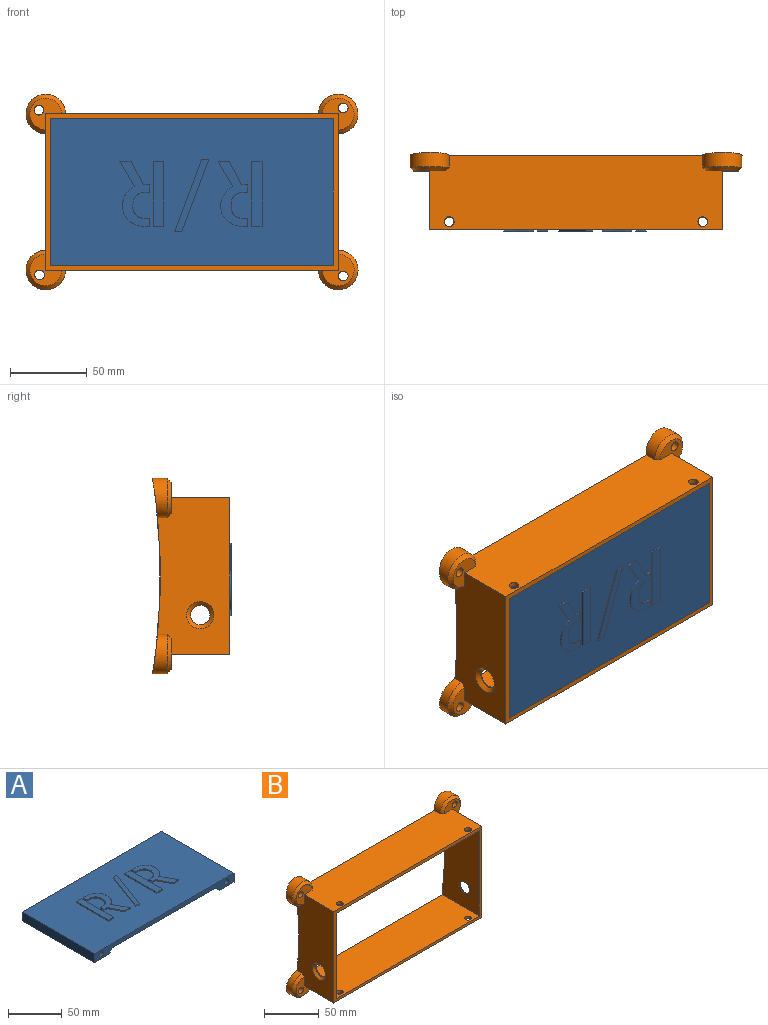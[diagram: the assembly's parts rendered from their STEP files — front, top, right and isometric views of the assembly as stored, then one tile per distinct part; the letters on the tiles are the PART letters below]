
ASSEMBLY  parts=2 mates=1
PART A: 82 faces, bbox 184.2x95.3x11.7 mm
  f0: plane 184.15x95.25mm, normal (0,0,1), area 16051.4mm2, adj f1,f6,f9,f10,f13,f14,f15,f16
  f1: plane 95.25x10.16mm, normal (-1,0,0), area 967.7mm2, adj f0,f2,f9,f10
  f2: plane 95.25x19.05mm, normal (0,0,-1), area 1814.5mm2, adj f1,f9,f10,f12
  f3: plane 135.89x95.25mm, normal (0,0,-1), area 12943.5mm2, adj f9,f10,f11,f12
  f4: plane 95.25x0.22mm, normal (-1,0,0), area 21mm2, adj f5,f9,f10,f11
  f5: plane 95.25x19.05mm, normal (0,0,-1), area 1814.5mm2, adj f4,f6,f9,f10
  f6: plane 95.25x10.38mm, normal (1,0,0), area 988.7mm2, adj f0,f5,f9,f10
  f7: cylinder r=3.17mm len=95.25mm, axis (0,1,0), area 1900.2mm2, adj f9,f10
  f8: cylinder r=3.17mm len=95.25mm, axis (0,1,0), area 1900.2mm2, adj f9,f10
  f9: plane 184.15x10.38mm, normal (0,-1,0), area 1095.7mm2, adj f0,f1,f2,f3,f4,f5,f6,f7
  f10: plane 184.15x10.38mm, normal (0,1,0), area 1095.7mm2, adj f0,f1,f2,f3,f4,f5,f6,f7
  f11: plane 95.25x5.08mm, normal (-0.71,0,-0.71), area 684.3mm2, adj f3,f4,f9,f10
  f12: plane 95.25x5.08mm, normal (0.71,0,-0.71), area 684.3mm2, adj f2,f3,f9,f10
  f13: plane 42.29x1.27mm, normal (-1,0,0), area 53.7mm2, adj f0,f14,f16,f17
  f14: plane 6.89x1.27mm, normal (0,-1,0), area 8.7mm2, adj f0,f13,f15,f17
  f15: plane 42.29x1.27mm, normal (1,0,0), area 53.7mm2, adj f0,f14,f16,f17
  f16: plane 6.89x1.27mm, normal (0,1,0), area 8.7mm2, adj f0,f13,f15,f17
  f17: plane 42.29x6.89mm, normal (0,0,1), area 291.2mm2, adj f13,f14,f15,f16
  f18: plane 16.65x9.64mm, normal (0.87,0.5,0), area 24.4mm2, adj f0,f19,f43,f44
  f19: extruded ~5.73x4.76mm, area 9.6mm2, adj f0,f18,f20,f44
  f20: extruded ~7.8x2.13mm, area 10.4mm2, adj f0,f19,f21,f44
  f21: extruded ~5.49x1.29mm, area 7.2mm2, adj f0,f20,f22,f44
  f22: extruded ~4.16x3.39mm, area 6.9mm2, adj f0,f21,f23,f44
  f23: extruded ~4.74x2.58mm, area 6.9mm2, adj f0,f22,f24,f44
  f24: extruded ~5.33x1.27mm, area 6.9mm2, adj f0,f23,f25,f44
  f25: plane 2.93x1.27mm, normal (0,1,0), area 3.7mm2, adj f0,f24,f26,f44
  f26: plane 5.22x1.27mm, normal (-1,0,0), area 6.6mm2, adj f0,f25,f27,f44
  f27: plane 2.81x1.27mm, normal (0,-1,0), area 3.6mm2, adj f0,f26,f28,f44
  f28: extruded ~4.25x1.27mm, area 5.6mm2, adj f0,f27,f29,f44
  f29: extruded ~2.49x2.07mm, area 4.1mm2, adj f0,f28,f30,f44
  f30: extruded ~2.58x1.27mm, area 3.6mm2, adj f0,f29,f31,f44
  f31: extruded ~2.39x1.27mm, area 3.1mm2, adj f0,f30,f32,f44
  f32: extruded ~4.33x1.27mm, area 5.6mm2, adj f0,f31,f33,f44
  f33: extruded ~2.73x1.67mm, area 4.1mm2, adj f0,f32,f34,f44
  f34: extruded ~2.3x1.4mm, area 3.4mm2, adj f0,f33,f35,f44
  f35: extruded ~2.52x1.27mm, area 3.3mm2, adj f0,f34,f36,f44
  f36: plane 3.9x1.27mm, normal (0,1,0), area 5mm2, adj f0,f35,f37,f44
  f37: plane 5.05x1.27mm, normal (-1,0,0), area 6.4mm2, adj f0,f36,f38,f44
  f38: plane 2.03x1.27mm, normal (0,-1,0), area 2.6mm2, adj f0,f37,f39,f44
  f39: plane 1.27x1.18mm, normal (0,-1,0), area 1.5mm2, adj f0,f38,f40,f44
  f40: extruded ~1.27x0.6mm, area 0.8mm2, adj f0,f39,f41,f44
  f41: extruded ~1.27x0.37mm, area 0.5mm2, adj f0,f40,f42,f44
  f42: plane 15.32x7.98mm, normal (-0.89,-0.46,0), area 21.9mm2, adj f0,f41,f43,f44
  f43: plane 7.29x1.27mm, normal (0,-1,0), area 9.3mm2, adj f0,f18,f42,f44
  f44: plane 42.29x19.46mm, normal (0,0,1), area 343.7mm2, adj f18,f19,f20,f21,f22,f23,f24,f25
  f45: plane 47.12x17.62mm, normal (0.94,-0.35,0), area 63.9mm2, adj f0,f46,f48,f49
  f46: plane 4.66x1.27mm, normal (0,1,0), area 5.9mm2, adj f0,f45,f47,f49
  f47: plane 47.12x17.61mm, normal (-0.94,0.35,0), area 63.9mm2, adj f0,f46,f48,f49
  f48: plane 4.65x1.27mm, normal (0,-1,0), area 5.9mm2, adj f0,f45,f47,f49
  f49: plane 47.12x22.27mm, normal (0,0,1), area 219.1mm2, adj f45,f46,f47,f48
  f50: plane 42.29x1.27mm, normal (-1,0,0), area 53.7mm2, adj f0,f51,f53,f54
  f51: plane 6.89x1.27mm, normal (0,-1,0), area 8.7mm2, adj f0,f50,f52,f54
  f52: plane 42.29x1.27mm, normal (1,0,0), area 53.7mm2, adj f0,f51,f53,f54
  f53: plane 6.89x1.27mm, normal (0,1,0), area 8.7mm2, adj f0,f50,f52,f54
  f54: plane 42.29x6.89mm, normal (0,0,1), area 291.2mm2, adj f50,f51,f52,f53
  f55: plane 16.65x9.64mm, normal (0.87,0.5,0), area 24.4mm2, adj f0,f56,f80,f81
  f56: extruded ~5.73x4.76mm, area 9.6mm2, adj f0,f55,f57,f81
  f57: extruded ~7.8x2.13mm, area 10.4mm2, adj f0,f56,f58,f81
  f58: extruded ~5.49x1.29mm, area 7.2mm2, adj f0,f57,f59,f81
  f59: extruded ~4.16x3.39mm, area 6.9mm2, adj f0,f58,f60,f81
  f60: extruded ~4.74x2.58mm, area 6.9mm2, adj f0,f59,f61,f81
  f61: extruded ~5.33x1.27mm, area 6.9mm2, adj f0,f60,f62,f81
  f62: plane 2.93x1.27mm, normal (0,1,0), area 3.7mm2, adj f0,f61,f63,f81
  f63: plane 5.22x1.27mm, normal (-1,0,0), area 6.6mm2, adj f0,f62,f64,f81
  f64: plane 2.81x1.27mm, normal (0,-1,0), area 3.6mm2, adj f0,f63,f65,f81
  f65: extruded ~4.25x1.27mm, area 5.6mm2, adj f0,f64,f66,f81
  f66: extruded ~2.49x2.07mm, area 4.1mm2, adj f0,f65,f67,f81
  f67: extruded ~2.58x1.27mm, area 3.6mm2, adj f0,f66,f68,f81
  f68: extruded ~2.39x1.27mm, area 3.1mm2, adj f0,f67,f69,f81
  f69: extruded ~4.33x1.27mm, area 5.6mm2, adj f0,f68,f70,f81
  f70: extruded ~2.73x1.67mm, area 4.1mm2, adj f0,f69,f71,f81
  f71: extruded ~2.3x1.4mm, area 3.4mm2, adj f0,f70,f72,f81
  f72: extruded ~2.52x1.27mm, area 3.3mm2, adj f0,f71,f73,f81
  f73: plane 3.9x1.27mm, normal (0,1,0), area 5mm2, adj f0,f72,f74,f81
  f74: plane 5.05x1.27mm, normal (-1,0,0), area 6.4mm2, adj f0,f73,f75,f81
  f75: plane 2.03x1.27mm, normal (0,-1,0), area 2.6mm2, adj f0,f74,f76,f81
  f76: plane 1.27x1.18mm, normal (0,-1,0), area 1.5mm2, adj f0,f75,f77,f81
  f77: extruded ~1.27x0.6mm, area 0.8mm2, adj f0,f76,f78,f81
  f78: extruded ~1.27x0.37mm, area 0.5mm2, adj f0,f77,f79,f81
  f79: plane 15.32x7.98mm, normal (-0.89,-0.46,0), area 21.9mm2, adj f0,f78,f80,f81
  f80: plane 7.29x1.27mm, normal (0,-1,0), area 9.3mm2, adj f0,f55,f79,f81
  f81: plane 42.29x19.46mm, normal (0,0,1), area 343.7mm2, adj f55,f56,f57,f58,f59,f60,f61,f62
PART B: 34 faces, bbox 216.1x50.1x127.2 mm
  f0: plane 190.5x48.29mm, normal (0,0,-1), area 8880.3mm2, adj f1,f2,f4,f11,f13,f14,f16,f17
  f1: plane 101.6x46.85mm, normal (-1,0,0), area 4202.2mm2, adj f0,f3,f4,f5,f7,f11,f13,f17
  f2: plane 101.6x46.85mm, normal (1,0,0), area 4202.2mm2, adj f0,f3,f4,f8,f10,f14,f16,f18
  f3: plane 190.5x48.29mm, normal (0,0,1), area 8880.3mm2, adj f1,f2,f4,f5,f7,f8,f10,f18
  f4: plane 190.5x101.6mm, normal (0,-1,0), area 1814.5mm2, adj f0,f1,f2,f3,f22,f23,f24,f25
  f5: cylinder r=12.82mm len=25.64mm, axis (0,1,0), area 489.4mm2, adj f1,f3,f19,f21
  f6: cylinder r=3.17mm len=10.95mm, axis (0,1,0), area 209.9mm2, adj f7,f21
  f7: plane 20.56x20.56mm, normal (0,-1,0), area 217.4mm2, adj f1,f3,f6,f19
  f8: cylinder r=12.82mm len=25.64mm, axis (0,1,0), area 489.4mm2, adj f2,f3,f18,f21
  f9: cylinder r=3.17mm len=11.17mm, axis (0,1,0), area 213.9mm2, adj f10,f21
  f10: plane 20.56x20.56mm, normal (0,-1,0), area 217.4mm2, adj f2,f3,f9,f18
  f11: cylinder r=12.82mm len=25.64mm, axis (0,1,0), area 489.4mm2, adj f0,f1,f17,f21
  f12: cylinder r=3.17mm len=11.05mm, axis (0,1,0), area 211.7mm2, adj f13,f21
  f13: plane 20.56x20.56mm, normal (0,-1,0), area 217.4mm2, adj f0,f1,f12,f17
  f14: cylinder r=12.82mm len=25.64mm, axis (0,1,0), area 489.4mm2, adj f0,f2,f20,f21
  f15: cylinder r=3.17mm len=11.17mm, axis (0,1,0), area 213.9mm2, adj f16,f21
  f16: plane 20.56x20.56mm, normal (0,-1,0), area 217.4mm2, adj f0,f2,f15,f20
  f17: cone r=12.82mm half-angle=45deg, axis (0,1,0), area 195.5mm2, adj f0,f1,f11,f13
  f18: cone r=12.82mm half-angle=45deg, axis (0,1,0), area 195.5mm2, adj f2,f3,f8,f10
  f19: cone r=12.82mm half-angle=45deg, axis (0,1,0), area 195.5mm2, adj f1,f3,f5,f7
  f20: cone r=12.82mm half-angle=45deg, axis (0,1,0), area 195.5mm2, adj f0,f2,f14,f16
  f21: cylinder r=399.46mm len=216.14mm, axis (-1,0,0), area 3259.9mm2, adj f0,f1,f2,f3,f5,f6,f8,f9
  f22: plane 184.15x47.89mm, normal (0,0,1), area 8755.9mm2, adj f4,f21,f23,f25,f30,f31
  f23: plane 95.25x47.89mm, normal (1,0,0), area 4253.9mm2, adj f4,f21,f22,f24,f27
  f24: plane 184.15x47.89mm, normal (0,0,-1), area 8755.9mm2, adj f4,f21,f23,f25,f28,f29
  f25: plane 95.25x47.89mm, normal (-1,0,0), area 4253.9mm2, adj f4,f21,f22,f24,f26
  f26: cylinder r=6.35mm len=12.7mm, axis (1,0,0), area 25.3mm2, adj f25,f33
  f27: cylinder r=6.35mm len=12.7mm, axis (1,0,0), area 25.3mm2, adj f23,f32
  f28: cylinder r=3.17mm len=6.35mm, axis (0,0,-1), area 63.3mm2, adj f3,f24
  f29: cylinder r=3.17mm len=6.35mm, axis (0,0,-1), area 63.3mm2, adj f3,f24
  f30: cylinder r=3.17mm len=6.35mm, axis (0,0,-1), area 63.3mm2, adj f0,f22
  f31: cylinder r=3.17mm len=6.35mm, axis (0,0,-1), area 63.3mm2, adj f0,f22
  f32: cone r=8.89mm half-angle=45deg, axis (-1,0,0), area 172mm2, adj f1,f27
  f33: cone r=6.35mm half-angle=45deg, axis (1,0,0), area 172mm2, adj f2,f26
PLACE A rot(axis=(0,-0.71,0.71),180deg) t=(-33.93,-54.32,96.72)mm
PLACE B t=(-33.93,-6.06,96.72)mm
MATE pin_slot A.f7 <-> B.f28  axis (0,0,-1) through (48.62,-51.78,49.1)mm
